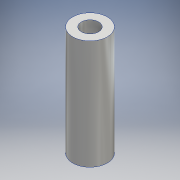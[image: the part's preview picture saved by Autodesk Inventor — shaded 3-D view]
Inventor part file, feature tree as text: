
AUTODESK INVENTOR PART (.ipt)
format: ipt  version: 2016 (Build 200138000, 138)  size: 115,712 bytes
history: native  units: mm
features: sketch x2, extrude x2, hole x2, other x1
ambient origin geometry x8: Origin, YZ Plane, XZ Plane, XY Plane, X Axis, Y Axis, Z Axis, Center Point
bodies: Body1 (feature_tree)
feature tree (7):
  other  "ソリッド1"
  sketch  "スケッチ1"
  extrude  "押し出し1"  Depth=6.0mm
  sketch  "スケッチ2"
  extrude  "押し出し2"  Depth=3.001mm
  hole  "穴1"  [1 undecoded]
  hole  "穴2"  [1 undecoded]
note: 2 required parameter values undecoded (feature->parameter linkage not recoverable at this tier; creation-order binding heuristic only, values carry confidence <= 0.55)
